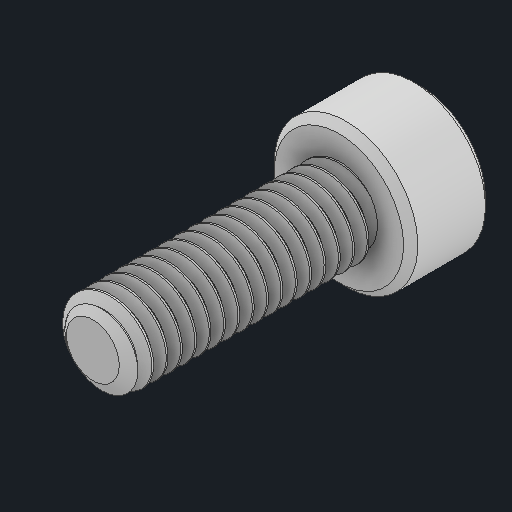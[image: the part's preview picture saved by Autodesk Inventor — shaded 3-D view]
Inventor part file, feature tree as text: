
AUTODESK INVENTOR PART (.ipt)
format: ipt  version: 2024 (Build 280153000, 153)  size: 609,792 bytes
history: native  units: in
note: dims shown in document units (in); Inventor stores cm internally (conversion verified against a paired STEP export)
features: chamfer x1
ambient origin geometry x8: Origin, YZ Plane, XZ Plane, XY Plane, X Axis, Y Axis, Z Axis, Center Point
bodies: Solid1 (feature_tree)
feature tree (1):
  chamfer  "Chamfer1"  [1 undecoded]
note: 1 required parameter value undecoded (feature->parameter linkage not recoverable at this tier; creation-order binding heuristic only, values carry confidence <= 0.55)
